# Revit family: Mixer-Basin-Dorf Jovian-Wall2
name_source: partatom
category: Plumbing Fixtures
revit_build: Autodesk Revit 2013 (Build: 20121003_2115(x64)
units: mm (PartAtom-declared; Revit-internal decimal feet)

## types (1)
- Jovian Wall Basin Mixer
    Assembly Code = C1030210
    CW Connection = Yes
    CWFU = 1.58
    Connector Radius = 10 mm  [stored 0.0328084 ft]
    Cost = 440.27 $
    Default Elevation = 900 mm  [stored 2.95276 ft]
    Description = Dorf Jovian Wall Basin Mixer
    HW Connection = Yes
    HWFU = 1.58
    Manufacturer = GWA Bathrooms & Kitchens
    Material_ANZRS = Metal-Chrome-Caroma
    Model = 2127.045A
    ModifiedIssue_ANZRS = 2013.2 $
    Type Comments = WELS 5 Star rated, 6L/min, 35mm adjustable cartridge, silicon aerator, Sure fit® installation
    URL = http://dorf.com.au
    Vent Connection = No
    Waste Connection = No

note: [stored X ft] marks values corroborated as IEEE doubles in the binary element streams (Revit-internal decimal feet)

## geometry (parser evidence)
native form markers: Blend x10, Sweep x1
no freeform markers — native parametric forms only
